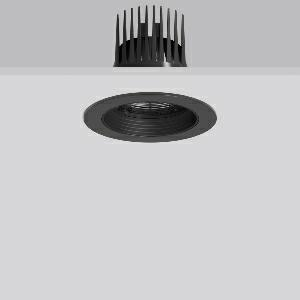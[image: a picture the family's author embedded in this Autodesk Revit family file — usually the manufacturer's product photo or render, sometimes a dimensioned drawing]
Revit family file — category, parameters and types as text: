
# Revit family: heledon_maxi_e_901761_003_4414
name_source: partatom
category: Lighting Fixtures
units: mm (PartAtom-declared; Revit-internal decimal feet)

## family parameters
Cut with Voids When Loaded = No
Host = Face
Light Source = No
Part Type = Normal
Room Calculation Point = No
Round Connector Dimension = Use Diameter
Shared = No

## types (1)
- HELEDON maxi E (1 x LED Modul 930, 2750 lm, 3000)
    Apparent Load = 25 VA
    Approval mark = CE
    CIE Flux Codes = 96 100 100 100 100
    Color Rendering = 90
    Color Temperature = 3000
    Default Elevation = 1800 mm
    Description = Series: HELEDON maxi
Round recessed downlight. Housing: die-cast aluminium, powder-coated. Black plastic ring and recessed LED to prevent glare from the side. Optical assembly with lens made of plastic (polycarbonate) for the best homogeneous light distribution - can be changed without tools. Best colour rendering index Ra>90. Suitable for Recessed ceiling mounting. Installation without tools thanks to spring fastening system. Including separate LED converter with connecting cable 600 mm.High quality converter without flickering and stroboscopic effect. Through-wiring box (5 pole) available as accessory. The following accessories can be mounted without use of tools: interchangeable lenses, decorative glasses, honeycomb louvre, clear and frosted diffusers, white interchangeable plastic ring. 
Colour: deep black, matt (RAL 9005)
Diameter: 162 mm
Height: 3 mm
Cut-out diameter: 152 mm
Recess height: 200 mm
Luminaire: recess height: 135 mm
Lamp: LED
Socket: without socket
Colour temperature: 3000K
Colour rendering index (CRI): 92
System power: 25 W
Rated luminous flux: 2750 lm
Luminous efficiency: 110 lm/W
Control gear: Regulated power supply
Protection class: II
Type of protection: IP 20
    Height = 0 mm  [stored 0 ft]
    Lamp = 1 x LED Modul 930
    Lamp Light Flux = 2750 lm
    Lamp count = 1
    Length = 162 mm
    Lifetime = 50000 h
    Luminous efficacy = 110 lm/W
    Manufacturer = RZB
    ModVariant = No
    Model = 901761.003
    Mounting Place = Ceiling
    Mounting Type = Recessed
    Number of Poles = 1
    OnlyDefault = Yes
    Power Factor = 1
    Product Name = HELEDON maxi E
    Product group = Recessed downlights
    ProductGroupID = 402
    Protection Class = Protection class II
    Protection Degree = IP 20
    RLX_Detail_Level = 1
    RLX_Emergency_Light_Flux = 0 lm
    RLX_Emergency_Type = 0
    RLX_Emergency_Type_DB = No
    RlxData = <blob elided: 121593 chars, md5=80500192>
    Socket = socket
    Standby Power = 0 W
    System Light Flux = 2750 lm
    System Power = 25 W
    Type Comments = Product without accessories
    Type Image = 901663.003.jpg
    URL = http://relux.com
    VarID = ---
    Voltage = 230 V
    Voltage Range = 220-240 V
    Weight = 0.00 kg
    Width = 0 mm  [stored 0 ft]

note: [stored X ft] marks values corroborated as IEEE doubles in the binary element streams (Revit-internal decimal feet)

## geometry (parser evidence)
native form markers: Blend x4, Sweep x12
no freeform markers — native parametric forms only
